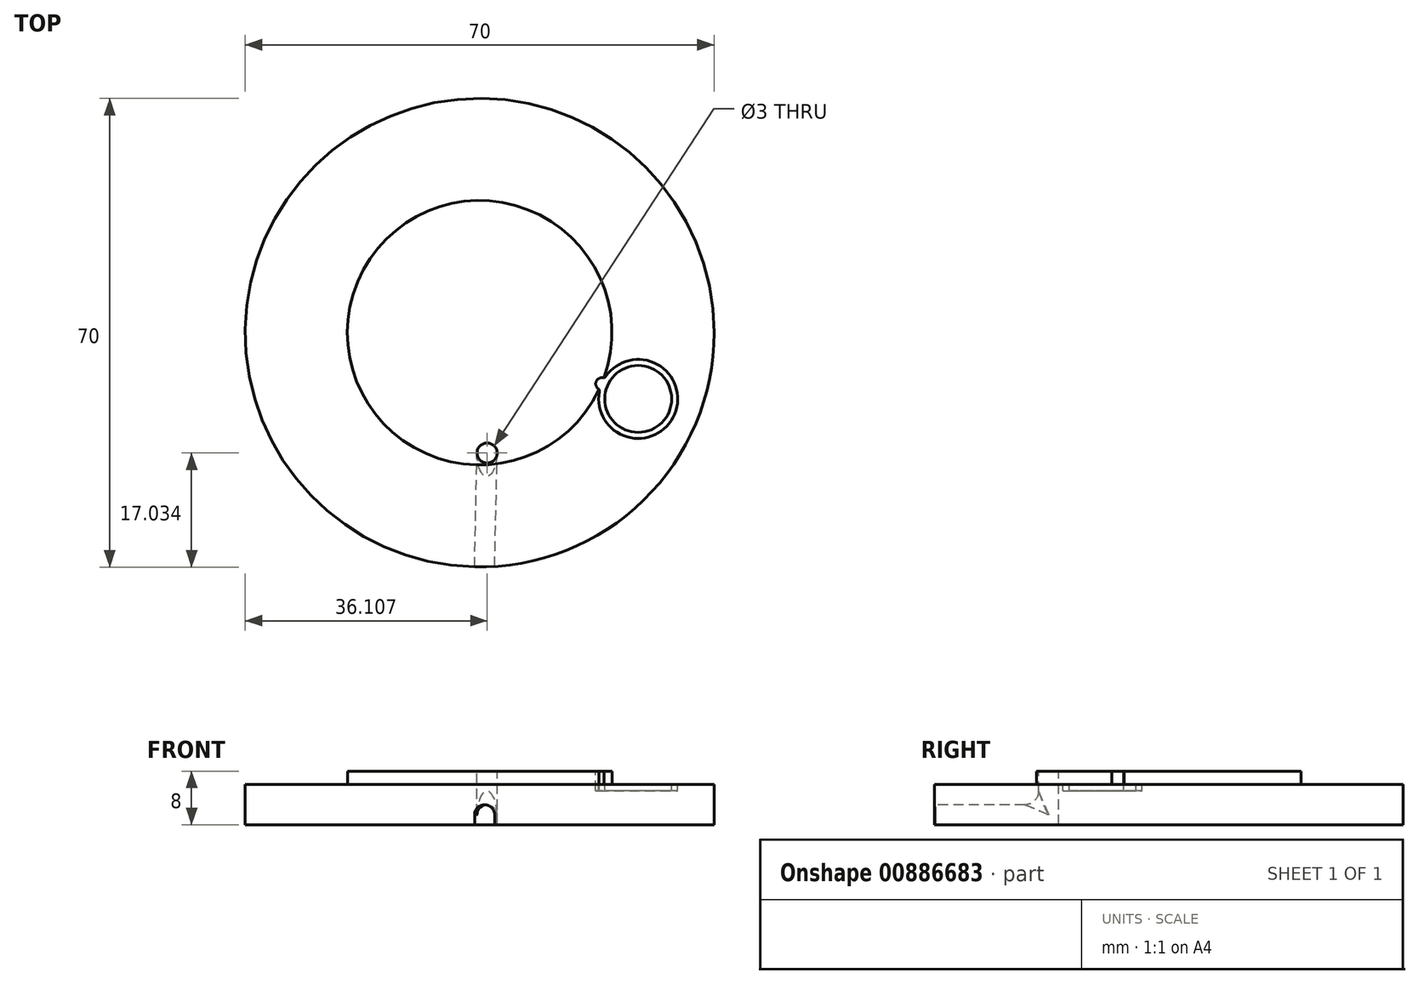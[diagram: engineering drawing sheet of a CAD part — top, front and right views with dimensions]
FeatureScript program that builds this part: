
annotation { "Feature Type Name" : "Feature", "Feature Type Description" : "" }
export const myFeature = defineFeature(function(context is Context, id is Id, definition is map)
    precondition{}
    {
        {
            var Q0;
            Q0=qCreatedBy(makeId("Top.planeOp"),FACE);
            var sketch = newSketch(context, id + "F0", { "sketchPlane" : qUnion([Q0])});
            skCircle(sketch, "E0", {"center": v(0, 0) * mm, "radius": 35 * mm});
            skSolve(sketch);
        }
        {
            var Q0;
            Q0=makeQuery(id+"F0.imprint","IMPRINT",FACE,{"disambiguationData":[TD([[makeQuery(id+"F0.imprint","IMPRINT",EDGE,{"derivedFrom":sQuery(id+"F0.wireOp",EDGE,"E0")}),1.0]])]});
            extrude(context, id + "F1", {"entities" : qUnion([Q0]), "depth" : 6 * mm, "offsetDistance" : 25 * mm});
        }
        {
            var Q0;
            Q0=makeQuery(id+"F1.opExtrude","CAP_FACE",FACE,{"disambiguationData":[OSD([sQuery(id+"F0.wireOp",EDGE,"E0")])],"isStart":false});
            var sketch = newSketch(context, id + "F2", { "sketchPlane" : qUnion([Q0])});
            skCircle(sketch, "E1", {"center": v(0, 0) * mm, "radius": 19.75 * mm});
            skSolve(sketch);
        }
        {
            var Q0;
            Q0=makeQuery(id+"F2.imprint","IMPRINT",FACE,{"disambiguationData":[TD([[makeQuery(id+"F2.imprint","IMPRINT",EDGE,{"derivedFrom":sQuery(id+"F2.wireOp",EDGE,"E1")}),1.0]])]});
            extrude(context, id + "F3", {"entities" : qUnion([Q0]), "operationType" : NewBodyOperationType.ADD, "depth" : 2 * mm, "offsetDistance" : 25 * mm});
        }
        {
            var Q0;
            Q0=makeQuery(id+"F3.opExtrude","CAP_FACE",FACE,{"disambiguationData":[OSD([sQuery(id+"F2.wireOp",EDGE,"E1")])],"isStart":false});
            var sketch = newSketch(context, id + "F4", { "sketchPlane" : qUnion([Q0])});
            skCircle(sketch, "E2", {"center": v(1.1, -17.97) * mm, "radius": 1.5 * mm});
            skSolve(sketch);
        }
        {
            var Q0;
            Q0=makeQuery(id+"F4.imprint","IMPRINT",FACE,{"disambiguationData":[TD([[makeQuery(id+"F4.imprint","IMPRINT",EDGE,{"derivedFrom":sQuery(id+"F4.wireOp",EDGE,"E2")}),1.0]])]});
            var Q1;
            Q1=makeQuery(id+"F1.opExtrude","CAP_FACE",FACE,{"disambiguationData":[OSD([sQuery(id+"F0.wireOp",EDGE,"E0")])],"isStart":true});
            extrude(context, id + "F5", {"entities" : qUnion([Q0]), "operationType" : NewBodyOperationType.REMOVE, "endBound" : BoundingType.UP_TO_SURFACE, "oppositeDirection" : true, "depth" : 25 * mm, "endBoundEntityFace" : qUnion([Q1]), "offsetDistance" : 25 * mm});
        }
        {
            var Q0;
            Q0=makeQuery(id+"F1.opExtrude","CAP_FACE",FACE,{"disambiguationData":[OSD([sQuery(id+"F0.wireOp",EDGE,"E0")])],"isStart":true});
            var sketch = newSketch(context, id + "F6", { "sketchPlane" : qUnion([Q0])});
            skLineSegment(sketch, "E3", {"start": v(2.24, 34.93) * mm, "end": v(2.6, 18) * mm});
            skLineSegment(sketch, "E4", {"start": v(-0.77, 35) * mm, "end": v(-0.4, 17.93) * mm});
            skSolve(sketch);
        }
        {
            var Q0;
            {var subQ0=sQuery(id+"F6.wireOp",EDGE,"E3");Q0=makeQuery(id+"F6.imprint","IMPRINT",FACE,{"disambiguationData":[TD([[makeQuery(id+"F6.imprint","IMPRINT",EDGE,{"derivedFrom":subQ0}),-1.0]])]});}
            extrude(context, id + "F7", {"entities" : qUnion([Q0]), "operationType" : NewBodyOperationType.REMOVE, "oppositeDirection" : true, "depth" : 3 * mm, "offsetDistance" : 25 * mm});
        }
        {
            var Q0;
            Q0=makeQuery(id+"F7.boolean.opBoolean","COPY",EDGE,{"derivedFrom":makeQuery(id+"F7.opExtrude","CAP_EDGE",EDGE,{"disambiguationData":[OSD([sQuery(id+"F6.wireOp",EDGE,"E3")])],"isStart":false})});
            var Q1;
            Q1=makeQuery(id+"F7.boolean.opBoolean","COPY",EDGE,{"derivedFrom":makeQuery(id+"F7.opExtrude","CAP_EDGE",EDGE,{"disambiguationData":[OSD([sQuery(id+"F6.wireOp",EDGE,"E4")])],"isStart":false})});
            fillet(context, id + "F8", {"entities" : qUnion([Q0, Q1]), "radius" : 1.5 * mm, "allowEdgeOverflow" : false});
        }
        {
            var Q0;
            Q0=makeQuery(id+"F8.opFillet","BLEND_EDGE",EDGE,{"blendedFrom":[makeQuery(id+"F7.boolean.opBoolean","COPY",EDGE,{"derivedFrom":makeQuery(id+"F7.opExtrude","CAP_EDGE",EDGE,{"disambiguationData":[OSD([sQuery(id+"F6.wireOp",EDGE,"E3")])],"isStart":false})}),makeQuery(id+"F5.boolean.opBoolean","COPY",FACE,{"derivedFrom":makeQuery(id+"F5.opExtrude","SWEPT_FACE",FACE,{"disambiguationData":[OSD([sQuery(id+"F4.wireOp",EDGE,"E2")])]})})],"blendedInto":[makeQuery(id+"F5.boolean.opBoolean","COPY",FACE,{"derivedFrom":makeQuery(id+"F5.opExtrude","SWEPT_FACE",FACE,{"disambiguationData":[OSD([sQuery(id+"F4.wireOp",EDGE,"E2")])]})})]});
            fillet(context, id + "F9", {"entities" : qUnion([Q0]), "radius" : 2 * mm, "tangentPropagation" : true, "allowEdgeOverflow" : false});
        }
        {
            var Q0;
            Q0=makeQuery(id+"F3.opExtrude","CAP_FACE",FACE,{"disambiguationData":[OSD([sQuery(id+"F2.wireOp",EDGE,"E1")])],"isStart":false});
            var sketch = newSketch(context, id + "F10", { "sketchPlane" : qUnion([Q0])});
            skCircle(sketch, "E5", {"center": v(23.67, -9.9) * mm, "radius": 5.9 * mm});
            skPoint(sketch, "E6", {"position": v(18.22, -7.62) * mm});
            skPoint(sketch, "E7", {"position": v(1.1, -17.97) * mm});
            skCircle(sketch, "E8", {"center": v(18.22, -7.62) * mm, "radius": 0.9 * mm});
            skCircle(sketch, "E9", {"center": v(23.67, -9.9) * mm, "radius": 5 * mm});
            skSolve(sketch);
        }
        {
            var Q0;
            {var subQ0=sQuery(id+"F10.wireOp",EDGE,"E8");var subQ1=makeQuery(id+"F3.opExtrude","CAP_EDGE",EDGE,{"disambiguationData":[OSD([sQuery(id+"F2.wireOp",EDGE,"E1")])],"isStart":false});var subQ2=makeQuery(id+"F10.imprint","INTERSECT",VERTEX,{"disambiguationData":[OD(0.0)],"derivedFrom":[subQ1,subQ0]});Q0=makeQuery(id+"F10.imprint","IMPRINT",FACE,{"disambiguationData":[TD([[makeQuery(id+"F10.imprint","IMPRINT",EDGE,{"disambiguationData":[TD([[subQ2,-1.0]])],"derivedFrom":subQ0}),1.0]])]});}
            var Q1;
            Q1=sQuery(id+"F10.wireOp",EDGE,"E8");
            extrude(context, id + "F11", {"entities" : qUnion([Q0]), "operationType" : NewBodyOperationType.REMOVE, "surfaceEntities" : qUnion([Q1]), "oppositeDirection" : true, "depth" : 2.9 * mm, "offsetDistance" : 25 * mm});
        }
        {
            var Q0;
            Q0=makeQuery(id+"F1.opExtrude","CAP_FACE",FACE,{"disambiguationData":[OSD([sQuery(id+"F0.wireOp",EDGE,"E0")])],"isStart":false});
            var sketch = newSketch(context, id + "F12", { "sketchPlane" : qUnion([Q0])});
            skCircle(sketch, "E10", {"center": v(23.67, -9.9) * mm, "radius": 5.9 * mm});
            skPoint(sketch, "E11", {"position": v(18.22, -7.62) * mm});
            skPoint(sketch, "E12", {"position": v(1.1, -17.97) * mm});
            skCircle(sketch, "E13", {"center": v(18.22, -7.62) * mm, "radius": 0.9 * mm});
            skCircle(sketch, "E14", {"center": v(23.67, -9.9) * mm, "radius": 5 * mm});
            skSolve(sketch);
        }
        {
            var Q0;
            {var subQ0=sQuery(id+"F12.wireOp",EDGE,"E13");var subQ6=makeQuery(id+"F12.imprint","INTERSECT",VERTEX,{"derivedFrom":[subQ0,sQuery(id+"F12.wireOp",EDGE,"E14")]});Q0=makeQuery(id+"F12.imprint","IMPRINT",FACE,{"disambiguationData":[TD([[makeQuery(id+"F12.imprint","IMPRINT",EDGE,{"disambiguationData":[TD([[subQ6,1.0]])],"derivedFrom":subQ0}),1.0]])]});}
            var Q1;
            {var subQ0=sQuery(id+"F12.wireOp",EDGE,"E13");var subQ1=sQuery(id+"F12.wireOp",EDGE,"E10");var subQ2=makeQuery(id+"F12.imprint","INTERSECT",VERTEX,{"disambiguationData":[OD(1.0)],"derivedFrom":[subQ1,subQ0]});Q1=makeQuery(id+"F12.imprint","IMPRINT",FACE,{"disambiguationData":[TD([[makeQuery(id+"F12.imprint","IMPRINT",EDGE,{"disambiguationData":[TD([[subQ2,1.0]])],"derivedFrom":subQ1}),-1.0]])]});}
            var Q2;
            {var subQ0=sQuery(id+"F12.wireOp",EDGE,"E13");var subQ1=sQuery(id+"F12.wireOp",EDGE,"E10");var subQ2=makeQuery(id+"F12.imprint","INTERSECT",VERTEX,{"disambiguationData":[OD(0.0)],"derivedFrom":[subQ1,subQ0]});Q2=makeQuery(id+"F12.imprint","IMPRINT",FACE,{"disambiguationData":[TD([[makeQuery(id+"F12.imprint","IMPRINT",EDGE,{"disambiguationData":[TD([[subQ2,-1.0]])],"derivedFrom":subQ1}),-1.0]])]});}
            var Q3;
            {var subQ4=sQuery(id+"F12.wireOp",EDGE,"E14");Q3=makeQuery(id+"F12.imprint","IMPRINT",FACE,{"disambiguationData":[TD([[makeQuery(id+"F12.imprint","IMPRINT",EDGE,{"derivedFrom":subQ4}),-1.0]])]});}
            var Q4;
            Q4=makeQuery(id+"F11.boolean.opBoolean","COPY",FACE,{"derivedFrom":makeQuery(id+"F11.opExtrude","CAP_FACE",FACE,{"disambiguationData":[OSD([sQuery(id+"F2.wireOp",EDGE,"E1"),sQuery(id+"F10.wireOp",EDGE,"E8")])],"isStart":false})});
            extrude(context, id + "F13", {"entities" : qUnion([Q0, Q1, Q2, Q3]), "operationType" : NewBodyOperationType.REMOVE, "endBound" : BoundingType.UP_TO_SURFACE, "oppositeDirection" : true, "depth" : 25 * mm, "endBoundEntityFace" : qUnion([Q4]), "offsetDistance" : 25 * mm});
        }
        {
            var Q0;
            {var subQ0=sQuery(id+"F12.wireOp",EDGE,"E13");var subQ1=sQuery(id+"F12.wireOp",EDGE,"E10");Q0=makeQuery(id+"F13.boolean.opBoolean","COPY",EDGE,{"derivedFrom":makeQuery(id+"F13.opExtrude","SWEPT_EDGE",EDGE,{"disambiguationData":[OSD([subQ1,subQ0]),TDD([makeQuery(id+"F12.imprint","INTERSECT",VERTEX,{"disambiguationData":[OD(1.0)],"derivedFrom":[subQ1,subQ0]})])]})});}
            var Q1;
            {var subQ0=sQuery(id+"F12.wireOp",EDGE,"E13");var subQ1=sQuery(id+"F12.wireOp",EDGE,"E10");Q1=makeQuery(id+"F13.boolean.opBoolean","COPY",EDGE,{"derivedFrom":makeQuery(id+"F13.opExtrude","SWEPT_EDGE",EDGE,{"disambiguationData":[OSD([subQ1,subQ0]),TDD([makeQuery(id+"F12.imprint","INTERSECT",VERTEX,{"disambiguationData":[OD(0.0)],"derivedFrom":[subQ1,subQ0]})])]})});}
            fillet(context, id + "F14", {"entities" : qUnion([Q0, Q1]), "radius" : 0.5 * mm, "tangentPropagation" : true, "allowEdgeOverflow" : false});
        }
    });
